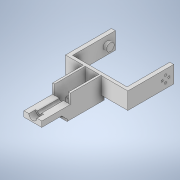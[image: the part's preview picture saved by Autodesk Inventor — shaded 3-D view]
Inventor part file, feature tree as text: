
AUTODESK INVENTOR PART (.ipt)
format: ipt  version: 2022 (Build 260153000, 153)  size: 238,080 bytes
history: native  units: mm
features: extrude x12, sketch x12, plane x1
ambient origin geometry x8: Origin, YZ Plane, XZ Plane, XY Plane, X Axis, Y Axis, Z Axis, Center Point
bodies: Solid1 (feature_tree)
feature tree (25):
  extrude  "Extrusion1"  Depth=25.4mm TaperAngle=0.0deg
  extrude  "Extrusion2"  Depth=3.0mm
  extrude  "Extrusion3"  Depth=46.0mm
  extrude  "Extrusion4"  Depth=34.33mm
  extrude  "Extrusion5"  Depth=7.0mm
  extrude  "Extrusion6"  Depth=6.0mm
  extrude  "Extrusion7"  Depth=5.0mm
  extrude  "Extrusion8"  Depth=16.63mm
  extrude  "Extrusion9"  Depth=6.0mm
  extrude  "Extrusion10"  Depth=12.0mm
  extrude  "Extrusion13"  Depth=7.0mm
  extrude  "Extrusion14"  Depth=7.0mm TaperAngle=0.0deg
  plane  "Work Plane6"
  sketch  "Sketch1"  dims[d4=69.0mm d5=25.4mm d6=0.0mm]
  sketch  "Sketch2"  dims[d19=3.0mm d20=10.35mm]
  sketch  "Sketch3"  dims[d22=46.0mm d23=0.0mm d24=10.35mm]
  sketch  "Sketch4"  dims[d25=10.35mm d26=34.33mm]
  sketch  "Sketch5"  dims[d27=31.33mm d28=0.0mm d30=7.0mm]
  sketch  "Sketch6"  dims[d31=6.0mm d32=0.0mm d35=2.0mm]
  sketch  "Sketch7"  dims[d36=0.0mm d37=0.0mm d41=5.0mm]
  sketch  "Sketch8"  dims[d42=16.63mm d46=30.0mm]
  sketch  "Sketch9"  dims[d47=10.0mm d48=0.0mm d49=6.0mm]
  sketch  "Sketch10"  dims[d50=0.0mm d51=0.0mm d52=12.0mm]
  sketch  "Sketch13"  dims[d53=10.0mm d54=0.0mm d55=7.0mm]
  sketch  "Sketch14"  dims[d56=7.0mm d57=7.0mm d58=5.0mm d59=0.0mm d60=0.0mm d61=7.0mm d62=0.0mm d76=11.5mm d77=5.0mm d78=0.0mm d80=3.0mm d81=40.0mm d83=360.0deg d85=5.0mm d86=0.0mm d87=-10.0mm]
